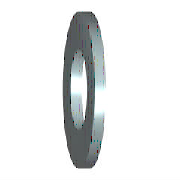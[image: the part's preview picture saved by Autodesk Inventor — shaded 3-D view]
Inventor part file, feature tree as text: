
AUTODESK INVENTOR PART (.ipt)
format: ipt  version: 2019 (Build 230136000, 136)  size: 109,056 bytes
history: native  units: mm (DEFAULTED — no unit token found)
features: extrude x1, other x1, plane x1, sketch x1
ambient origin geometry x7: Origin, YZ Plane, XY Plane, X Axis, Y Axis, Z Axis, Center Point
bodies: Solid1 (feature_tree)
feature tree (4):
  extrude  "Cuerpo"  Depth=0.8mm
  other  "Work Axis1"
  plane  "Work Plane1"
  sketch  "Boceto"  dims[d0=4.3mm d1=9.0mm d2=0.8mm d3=0.0mm d4=0.0mm d5=0.0mm d6=0.0mm d7=0.0mm]
